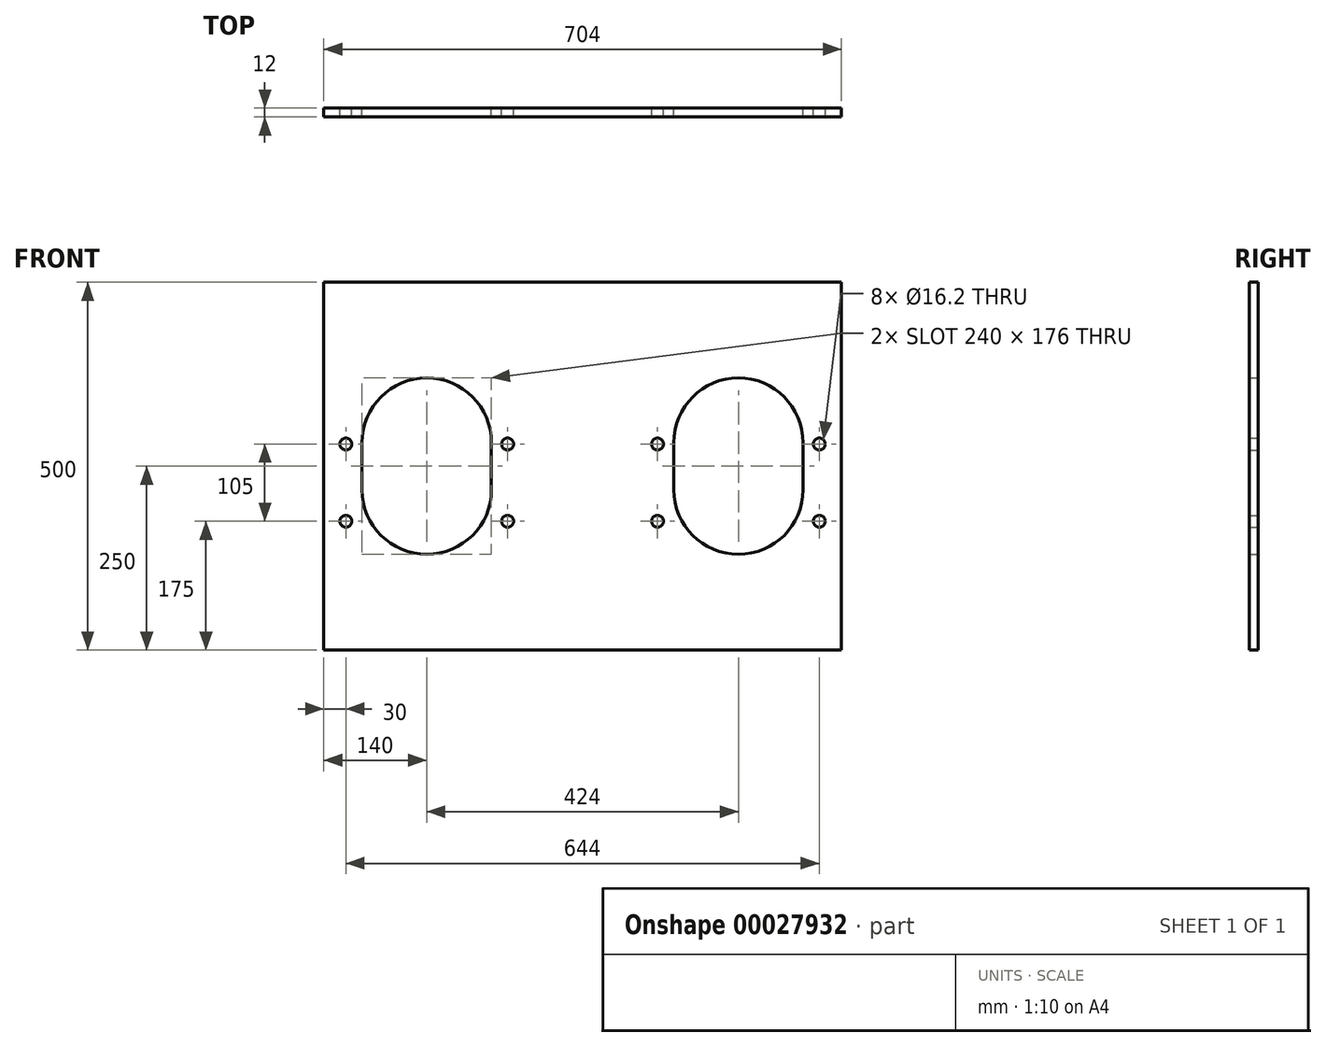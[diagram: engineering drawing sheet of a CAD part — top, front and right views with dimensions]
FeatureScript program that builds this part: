
annotation { "Feature Type Name" : "Feature", "Feature Type Description" : "" }
export const myFeature = defineFeature(function(context is Context, id is Id, definition is map)
    precondition{}
    {
        {
            var Q0;
            Q0=qCreatedBy(makeId("Front.planeOp"),FACE);
            var sketch = newSketch(context, id + "F0", { "sketchPlane" : qUnion([Q0])});
            skLineSegment(sketch, "E0.bottom", {"start": v(0, 0) * mm, "end": v(-704, 0) * mm});
            skLineSegment(sketch, "E0.top", {"start": v(0, 500) * mm, "end": v(-704, 500) * mm});
            skLineSegment(sketch, "E0.left", {"start": v(0, 0) * mm, "end": v(0, 500) * mm});
            skLineSegment(sketch, "E0.right", {"start": v(-704, 0) * mm, "end": v(-704, 500) * mm});
            skLineSegment(sketch, "E1", {"start": v(-704, 410) * mm, "end": v(0, 410) * mm, "construction": true});
            skLineSegment(sketch, "E2", {"start": v(-704, 90) * mm, "end": v(0, 90) * mm, "construction": true});
            skLineSegment(sketch, "E3", {"start": v(-564, 500) * mm, "end": v(-564, 0) * mm, "construction": true});
            skLineSegment(sketch, "E4", {"start": v(-140, 500) * mm, "end": v(-140, 0) * mm, "construction": true});
            skLineSegment(sketch, "E5", {"start": v(-674, 500) * mm, "end": v(-674, 0) * mm, "construction": true});
            skLineSegment(sketch, "E6", {"start": v(-454, 500) * mm, "end": v(-454, 0) * mm, "construction": true});
            skLineSegment(sketch, "E7", {"start": v(-250, 500) * mm, "end": v(-250, 0) * mm, "construction": true});
            skLineSegment(sketch, "E8", {"start": v(-30, 500) * mm, "end": v(-30, 0) * mm, "construction": true});
            skLineSegment(sketch, "E9.bottom", {"start": v(-564, 370) * mm, "end": v(-564, 370) * mm});
            skLineSegment(sketch, "E9.top", {"start": v(-564, 130) * mm, "end": v(-564, 130) * mm});
            skLineSegment(sketch, "E9.left", {"start": v(-652, 282) * mm, "end": v(-652, 218) * mm});
            skLineSegment(sketch, "E9.right", {"start": v(-476, 282) * mm, "end": v(-476, 218) * mm});
            skLineSegment(sketch, "E10.bottom", {"start": v(-140, 370) * mm, "end": v(-140, 370) * mm});
            skLineSegment(sketch, "E10.top", {"start": v(-140, 130) * mm, "end": v(-140, 130) * mm});
            skLineSegment(sketch, "E10.left", {"start": v(-228, 282) * mm, "end": v(-228, 218) * mm});
            skLineSegment(sketch, "E10.right", {"start": v(-52, 282) * mm, "end": v(-52, 218) * mm});
            skPoint(sketch, "E11.visualSharp", {"position": v(-652, 370) * mm});
            skArc(sketch, "E11.filletArc", {"start": v(-564, 370) * mm, "mid": v(-626.23, 344.23) * mm, "end": v(-652, 282) * mm});
            skPoint(sketch, "E12.visualSharp", {"position": v(-476, 370) * mm});
            skArc(sketch, "E12.filletArc", {"start": v(-476, 282) * mm, "mid": v(-501.77, 344.23) * mm, "end": v(-564, 370) * mm});
            skPoint(sketch, "E13.visualSharp", {"position": v(-476, 130) * mm});
            skArc(sketch, "E13.filletArc", {"start": v(-564, 130) * mm, "mid": v(-501.77, 155.77) * mm, "end": v(-476, 218) * mm});
            skPoint(sketch, "E14.visualSharp", {"position": v(-652, 130) * mm});
            skArc(sketch, "E14.filletArc", {"start": v(-652, 218) * mm, "mid": v(-626.23, 155.77) * mm, "end": v(-564, 130) * mm});
            skPoint(sketch, "E15.visualSharp", {"position": v(-228, 370) * mm});
            skArc(sketch, "E15.filletArc", {"start": v(-140, 370) * mm, "mid": v(-202.23, 344.23) * mm, "end": v(-228, 282) * mm});
            skPoint(sketch, "E16.visualSharp", {"position": v(-52, 130) * mm});
            skArc(sketch, "E16.filletArc", {"start": v(-140, 130) * mm, "mid": v(-77.77, 155.77) * mm, "end": v(-52, 218) * mm});
            skPoint(sketch, "E17.visualSharp", {"position": v(-52, 370) * mm});
            skArc(sketch, "E17.filletArc", {"start": v(-52, 282) * mm, "mid": v(-77.77, 344.23) * mm, "end": v(-140, 370) * mm});
            skPoint(sketch, "E18.visualSharp", {"position": v(-228, 130) * mm});
            skArc(sketch, "E18.filletArc", {"start": v(-228, 218) * mm, "mid": v(-202.23, 155.77) * mm, "end": v(-140, 130) * mm});
            skCircle(sketch, "E19", {"center": v(-674, 280) * mm, "radius": 8.1 * mm});
            skCircle(sketch, "E20", {"center": v(-674, 175) * mm, "radius": 8.1 * mm});
            skCircle(sketch, "E21", {"center": v(-454, 280) * mm, "radius": 8.1 * mm});
            skCircle(sketch, "E22", {"center": v(-454, 175) * mm, "radius": 8.1 * mm});
            skCircle(sketch, "E23", {"center": v(-250, 280) * mm, "radius": 8.1 * mm});
            skCircle(sketch, "E24", {"center": v(-250, 175) * mm, "radius": 8.1 * mm});
            skCircle(sketch, "E25", {"center": v(-30, 280) * mm, "radius": 8.1 * mm});
            skCircle(sketch, "E26", {"center": v(-30, 175) * mm, "radius": 8.1 * mm});
            skSolve(sketch);
        }
        {
            var Q0;
            Q0=makeQuery(id+"F0.imprint","IMPRINT",FACE,{"disambiguationData":[TD([[makeQuery(id+"F0.imprint","IMPRINT",EDGE,{"derivedFrom":sQuery(id+"F0.wireOp",EDGE,"E0.bottom")}),-1.0]])]});
            var Q1;
            Q1 = qSketchRegion(id + "F2", true);
            extrude(context, id + "F1", {"entities" : qUnion([Q0, Q1]), "offsetDistance" : 25 * mm, "depth" : 12 * mm});
        }
    });
